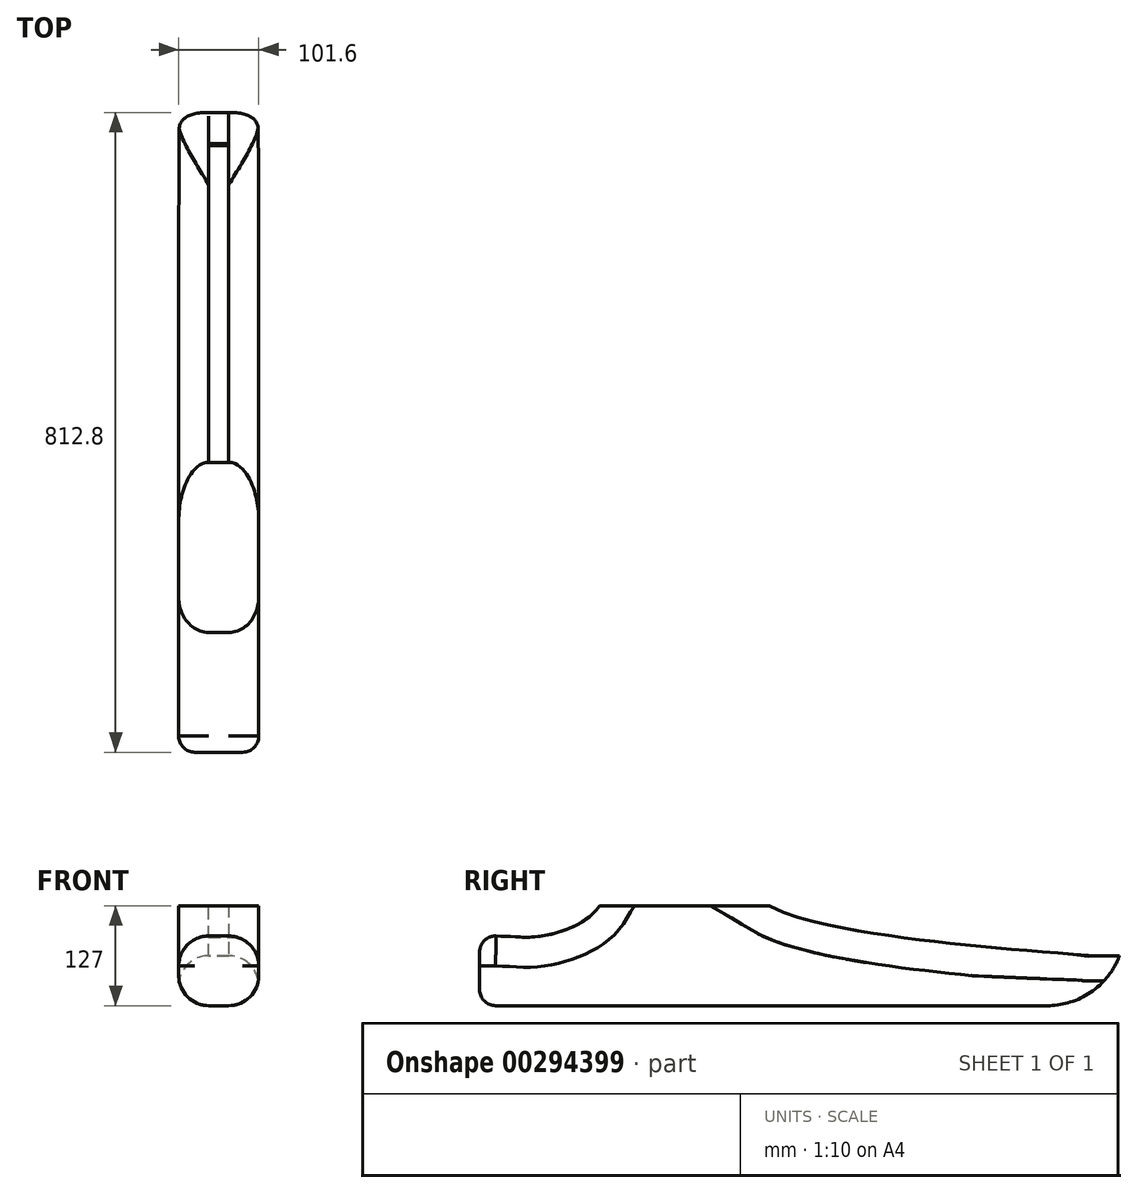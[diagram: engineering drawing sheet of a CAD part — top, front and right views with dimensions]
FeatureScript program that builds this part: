
annotation { "Feature Type Name" : "Feature", "Feature Type Description" : "" }
export const myFeature = defineFeature(function(context is Context, id is Id, definition is map)
    precondition{}
    {
        {
            var Q0;
            Q0=qCreatedBy(makeId("Right.planeOp"),FACE);
            var sketch = newSketch(context, id + "F0", { "sketchPlane" : qUnion([Q0])});
            skLineSegment(sketch, "E0.bottom", {"start": v(0, 119.4) * mm, "end": v(215.9, 119.4) * mm});
            skLineSegment(sketch, "E0.top", {"start": v(-152.2, -7.6) * mm, "end": v(660.6, -7.6) * mm});
            skLineSegment(sketch, "E0.left", {"start": v(-152.2, 81.3) * mm, "end": v(-152.2, -7.6) * mm});
            skLineSegment(sketch, "E0.right", {"start": v(660.6, 55.9) * mm, "end": v(660.6, -7.6) * mm});
            skPoint(sketch, "E1", {"position": v(660.6, 55.9) * mm});
            skPoint(sketch, "E2", {"position": v(-152.2, 81.3) * mm});
            skFitSpline(sketch, "E3", {"points": [v(660.6, 55.9) * mm, v(620.2, 55.9) * mm, v(215.9, 119.4) * mm], "startDerivative": vector(-781.33, -14.03) * mm, "endDerivative": vector(-301.92, 177.6) * mm});
            skFitSpline(sketch, "E4", {"points": [v(-152.2, 81.3) * mm, v(-70.4, 81.3) * mm, v(0, 119.4) * mm], "startDerivative": vector(258.58, 0) * mm, "endDerivative": vector(75.06, 126.98) * mm});
            skSolve(sketch);
        }
        {
            var Q0;
            Q0 = qSketchRegion(id + "F0", true);
            extrude(context, id + "F1", {"entities" : qUnion([Q0]), "depth" : 101.6 * mm, "offsetDistance" : 25.4 * mm});
        }
        {
            var Q0;
            Q0=makeQuery(id+"F1.opExtrude","CAP_EDGE",EDGE,{"disambiguationData":[OSD([sQuery(id+"F0.wireOp",EDGE,"E4")])],"isStart":false});
            var Q1;
            Q1=makeQuery(id+"F1.opExtrude","CAP_EDGE",EDGE,{"disambiguationData":[OSD([sQuery(id+"F0.wireOp",EDGE,"E4")])],"isStart":true});
            fillet(context, id + "F2", {"entities" : qUnion([Q0, Q1]), "radius" : 38.1 * mm, "tangentPropagation" : true, "allowEdgeOverflow" : false});
        }
        {
            var Q0;
            Q0=makeQuery(id+"F1.opExtrude","CAP_EDGE",EDGE,{"disambiguationData":[OSD([sQuery(id+"F0.wireOp",EDGE,"E0.top")])],"isStart":false});
            var Q1;
            Q1=makeQuery(id+"F1.opExtrude","CAP_EDGE",EDGE,{"disambiguationData":[OSD([sQuery(id+"F0.wireOp",EDGE,"E0.top")])],"isStart":true});
            fillet(context, id + "F3", {"entities" : qUnion([Q0, Q1]), "radius" : 38.1 * mm, "tangentPropagation" : true, "allowEdgeOverflow" : false});
        }
        {
            var Q0;
            Q0=makeQuery(id+"F1.opExtrude","CAP_EDGE",EDGE,{"disambiguationData":[OSD([sQuery(id+"F0.wireOp",EDGE,"E3")])],"isStart":false});
            var Q1;
            Q1=makeQuery(id+"F1.opExtrude","CAP_EDGE",EDGE,{"disambiguationData":[OSD([sQuery(id+"F0.wireOp",EDGE,"E3")])],"isStart":true});
            fillet(context, id + "F4", {"entities" : qUnion([Q0, Q1]), "radius" : 38.1 * mm, "tangentPropagation" : true, "allowEdgeOverflow" : false});
        }
        {
            var Q0;
            Q0=makeQuery(id+"F2.opFillet","BLEND_EDGE",EDGE,{"blendedFrom":[makeQuery(id+"F1.opExtrude","CAP_EDGE",EDGE,{"disambiguationData":[OSD([sQuery(id+"F0.wireOp",EDGE,"E4")])],"isStart":false}),makeQuery(id+"F1.opExtrude","SWEPT_FACE",FACE,{"disambiguationData":[OSD([sQuery(id+"F0.wireOp",EDGE,"E0.left")])]})],"blendedInto":[makeQuery(id+"F1.opExtrude","SWEPT_FACE",FACE,{"disambiguationData":[OSD([sQuery(id+"F0.wireOp",EDGE,"E0.left")])]})]});
            var Q1;
            Q1=makeQuery(id+"F2.opFillet","BLEND_EDGE",EDGE,{"blendedFrom":[makeQuery(id+"F1.opExtrude","CAP_EDGE",EDGE,{"disambiguationData":[OSD([sQuery(id+"F0.wireOp",EDGE,"E4")])],"isStart":true}),makeQuery(id+"F1.opExtrude","SWEPT_FACE",FACE,{"disambiguationData":[OSD([sQuery(id+"F0.wireOp",EDGE,"E0.left")])]})],"blendedInto":[makeQuery(id+"F1.opExtrude","SWEPT_FACE",FACE,{"disambiguationData":[OSD([sQuery(id+"F0.wireOp",EDGE,"E0.left")])]})]});
            var Q2;
            Q2=makeQuery(id+"F1.opExtrude","SWEPT_EDGE",EDGE,{"disambiguationData":[OSD([sQuery(id+"F0.wireOp",EDGE,"E0.left"),sQuery(id+"F0.wireOp",EDGE,"E4")])]});
            var Q3;
            Q3=makeQuery(id+"F3.opFillet","BLEND_EDGE",EDGE,{"blendedFrom":[makeQuery(id+"F1.opExtrude","CAP_EDGE",EDGE,{"disambiguationData":[OSD([sQuery(id+"F0.wireOp",EDGE,"E0.top")])],"isStart":false}),makeQuery(id+"F1.opExtrude","SWEPT_FACE",FACE,{"disambiguationData":[OSD([sQuery(id+"F0.wireOp",EDGE,"E0.left")])]})],"blendedInto":[makeQuery(id+"F1.opExtrude","SWEPT_FACE",FACE,{"disambiguationData":[OSD([sQuery(id+"F0.wireOp",EDGE,"E0.left")])]})]});
            var Q4;
            Q4=makeQuery(id+"F1.opExtrude","CAP_EDGE",EDGE,{"disambiguationData":[OSD([sQuery(id+"F0.wireOp",EDGE,"E0.left")])],"isStart":false});
            var Q5;
            Q5=makeQuery(id+"F3.opFillet","BLEND_EDGE",EDGE,{"blendedFrom":[makeQuery(id+"F1.opExtrude","CAP_EDGE",EDGE,{"disambiguationData":[OSD([sQuery(id+"F0.wireOp",EDGE,"E0.top")])],"isStart":true}),makeQuery(id+"F1.opExtrude","SWEPT_FACE",FACE,{"disambiguationData":[OSD([sQuery(id+"F0.wireOp",EDGE,"E0.left")])]})],"blendedInto":[makeQuery(id+"F1.opExtrude","SWEPT_FACE",FACE,{"disambiguationData":[OSD([sQuery(id+"F0.wireOp",EDGE,"E0.left")])]})]});
            var Q6;
            Q6=makeQuery(id+"F1.opExtrude","CAP_EDGE",EDGE,{"disambiguationData":[OSD([sQuery(id+"F0.wireOp",EDGE,"E0.left")])],"isStart":true});
            fillet(context, id + "F5", {"entities" : qUnion([Q0, Q1, Q2, Q3, Q4, Q5, Q6]), "radius" : 20.24 * mm, "tangentPropagation" : true, "allowEdgeOverflow" : false});
        }
        {
            var Q0;
            Q0=makeQuery(id+"F3.opFillet","BLEND_EDGE",EDGE,{"blendedFrom":[makeQuery(id+"F1.opExtrude","CAP_EDGE",EDGE,{"disambiguationData":[OSD([sQuery(id+"F0.wireOp",EDGE,"E0.top")])],"isStart":true}),makeQuery(id+"F1.opExtrude","SWEPT_FACE",FACE,{"disambiguationData":[OSD([sQuery(id+"F0.wireOp",EDGE,"E0.right")])]})],"blendedInto":[makeQuery(id+"F1.opExtrude","SWEPT_FACE",FACE,{"disambiguationData":[OSD([sQuery(id+"F0.wireOp",EDGE,"E0.right")])]})]});
            var Q1;
            Q1=makeQuery(id+"F1.opExtrude","SWEPT_EDGE",EDGE,{"disambiguationData":[OSD([sQuery(id+"F0.wireOp",EDGE,"E0.top"),sQuery(id+"F0.wireOp",EDGE,"E0.right")])]});
            var Q2;
            Q2=makeQuery(id+"F3.opFillet","BLEND_EDGE",EDGE,{"blendedFrom":[makeQuery(id+"F1.opExtrude","CAP_EDGE",EDGE,{"disambiguationData":[OSD([sQuery(id+"F0.wireOp",EDGE,"E0.top")])],"isStart":false}),makeQuery(id+"F1.opExtrude","SWEPT_FACE",FACE,{"disambiguationData":[OSD([sQuery(id+"F0.wireOp",EDGE,"E0.right")])]})],"blendedInto":[makeQuery(id+"F1.opExtrude","SWEPT_FACE",FACE,{"disambiguationData":[OSD([sQuery(id+"F0.wireOp",EDGE,"E0.right")])]})]});
            fillet(context, id + "F6", {"entities" : qUnion([Q0, Q1, Q2]), "radius" : 98.11 * mm, "tangentPropagation" : true, "allowEdgeOverflow" : false});
        }
    });
